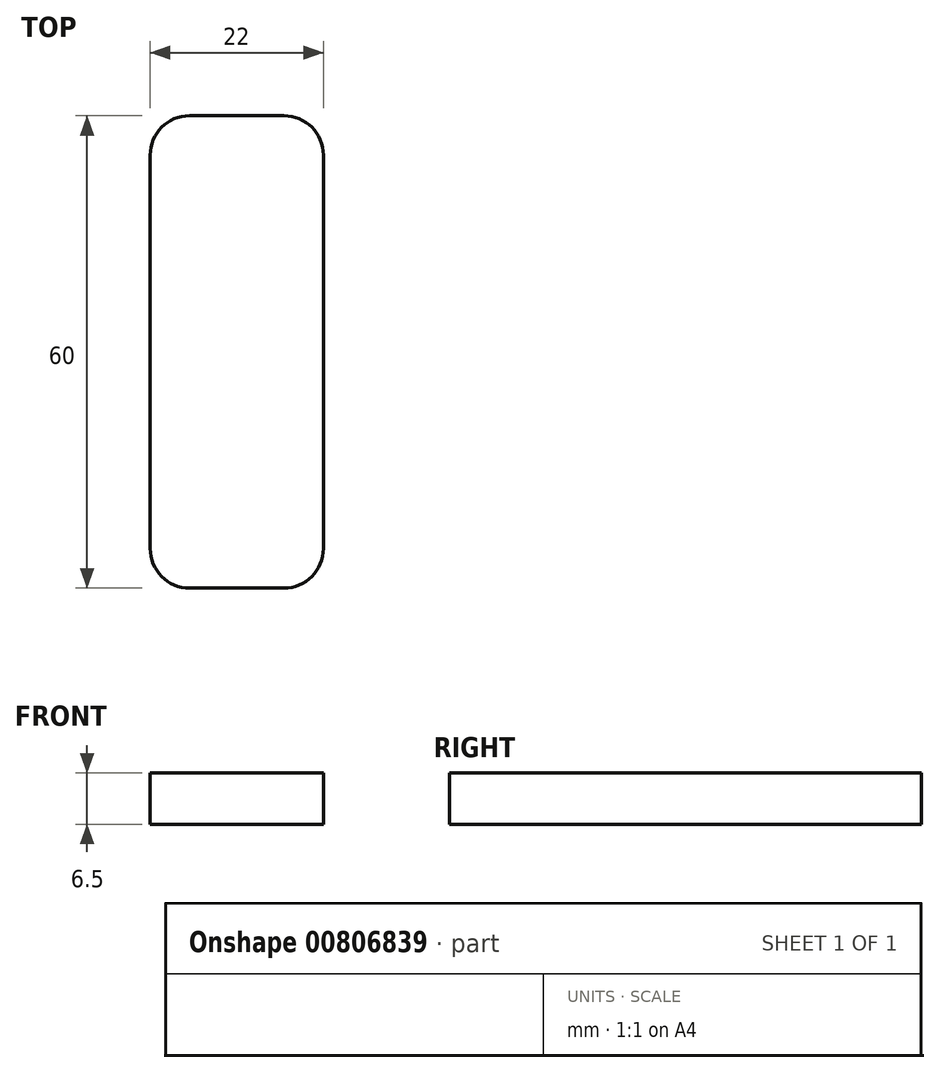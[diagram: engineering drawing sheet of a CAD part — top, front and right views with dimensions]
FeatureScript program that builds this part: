
annotation { "Feature Type Name" : "Feature", "Feature Type Description" : "" }
export const myFeature = defineFeature(function(context is Context, id is Id, definition is map)
    precondition{}
    {
        {
            var Q0;
            Q0=qCreatedBy(makeId("Top.planeOp"),FACE);
            var sketch = newSketch(context, id + "F0", { "sketchPlane" : qUnion([Q0])});
            skLineSegment(sketch, "E0.bottom", {"start": v(11, 30) * mm, "end": v(-11, 30) * mm});
            skLineSegment(sketch, "E0.top", {"start": v(11, -30) * mm, "end": v(-11, -30) * mm});
            skLineSegment(sketch, "E0.left", {"start": v(11, 30) * mm, "end": v(11, -30) * mm});
            skLineSegment(sketch, "E0.right", {"start": v(-11, 30) * mm, "end": v(-11, -30) * mm});
            skPoint(sketch, "E0.middle", {"position": v(0, 0) * mm});
            skSolve(sketch);
        }
        {
            var Q0;
            Q0=qSketchRegion(id+"F0",true);
            extrude(context, id + "F1", {"entities" : qUnion([Q0]), "depth" : 6.5 * mm, "offsetDistance" : 25 * mm});
        }
        {
            var Q0;
            Q0=makeQuery(id+"F1.opExtrude","SWEPT_EDGE",EDGE,{"disambiguationData":[OSD([sQuery(id+"F0.wireOp",EDGE,"E0.top"),sQuery(id+"F0.wireOp",EDGE,"E0.left")])]});
            var Q1;
            Q1=makeQuery(id+"F1.opExtrude","SWEPT_EDGE",EDGE,{"disambiguationData":[OSD([sQuery(id+"F0.wireOp",EDGE,"E0.top"),sQuery(id+"F0.wireOp",EDGE,"E0.right")])]});
            var Q2;
            Q2=makeQuery(id+"F1.opExtrude","SWEPT_EDGE",EDGE,{"disambiguationData":[OSD([sQuery(id+"F0.wireOp",EDGE,"E0.bottom"),sQuery(id+"F0.wireOp",EDGE,"E0.left")])]});
            var Q3;
            Q3=makeQuery(id+"F1.opExtrude","SWEPT_EDGE",EDGE,{"disambiguationData":[OSD([sQuery(id+"F0.wireOp",EDGE,"E0.bottom"),sQuery(id+"F0.wireOp",EDGE,"E0.right")])]});
            fillet(context, id + "F2", {"entities" : qUnion([Q0, Q1, Q2, Q3]), "radius" : 5 * mm, "tangentPropagation" : true, "allowEdgeOverflow" : false});
        }
    });
